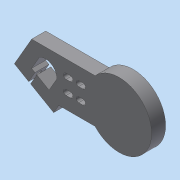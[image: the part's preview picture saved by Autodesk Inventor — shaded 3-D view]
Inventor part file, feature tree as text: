
AUTODESK INVENTOR PART (.ipt)
format: ipt  version: 2017 (Build 210142000, 142)  size: 156,160 bytes
history: native  units: in
note: dims shown in document units (in); Inventor stores cm internally (conversion verified against a paired STEP export)
features: extrude x4, plane x1, sketch x1
ambient origin geometry x8: Origin, YZ Plane, XZ Plane, XY Plane, X Axis, Y Axis, Z Axis, Center Point
bodies: Solid1 (feature_tree)
feature tree (6):
  extrude  "plate"  Depth=0.45in
  extrude  "tension holes"  Depth=0.72in
  plane  "Work Plane1"
  sketch  "Sketch2"  dims[d2=2.3228in d3=0.56in d4=0.72in d11=0.45in d20=0.7874in d22=0.5in d23=0.7874in d25=0.75in d48=0.0787in d49=0.5in d50=0.0in d54=0.2in d55=0.0in d56=0.41in d58=0.45in d59=30.0deg d60=0.1875in d63=-1.2in d67=1.0in d68=0.0in d70=0.19in d72=0.19in d73=0.15in d75=0.7874in d77=0.5in d78=0.7874in d80=0.45in d83=1.0in d84=0.0in d85=0.3504in d86=2.6394in d90=0.45in]
  extrude  "clamp screw"  Depth=0.45in
  extrude  "clamp nut"  Depth=0.5in
